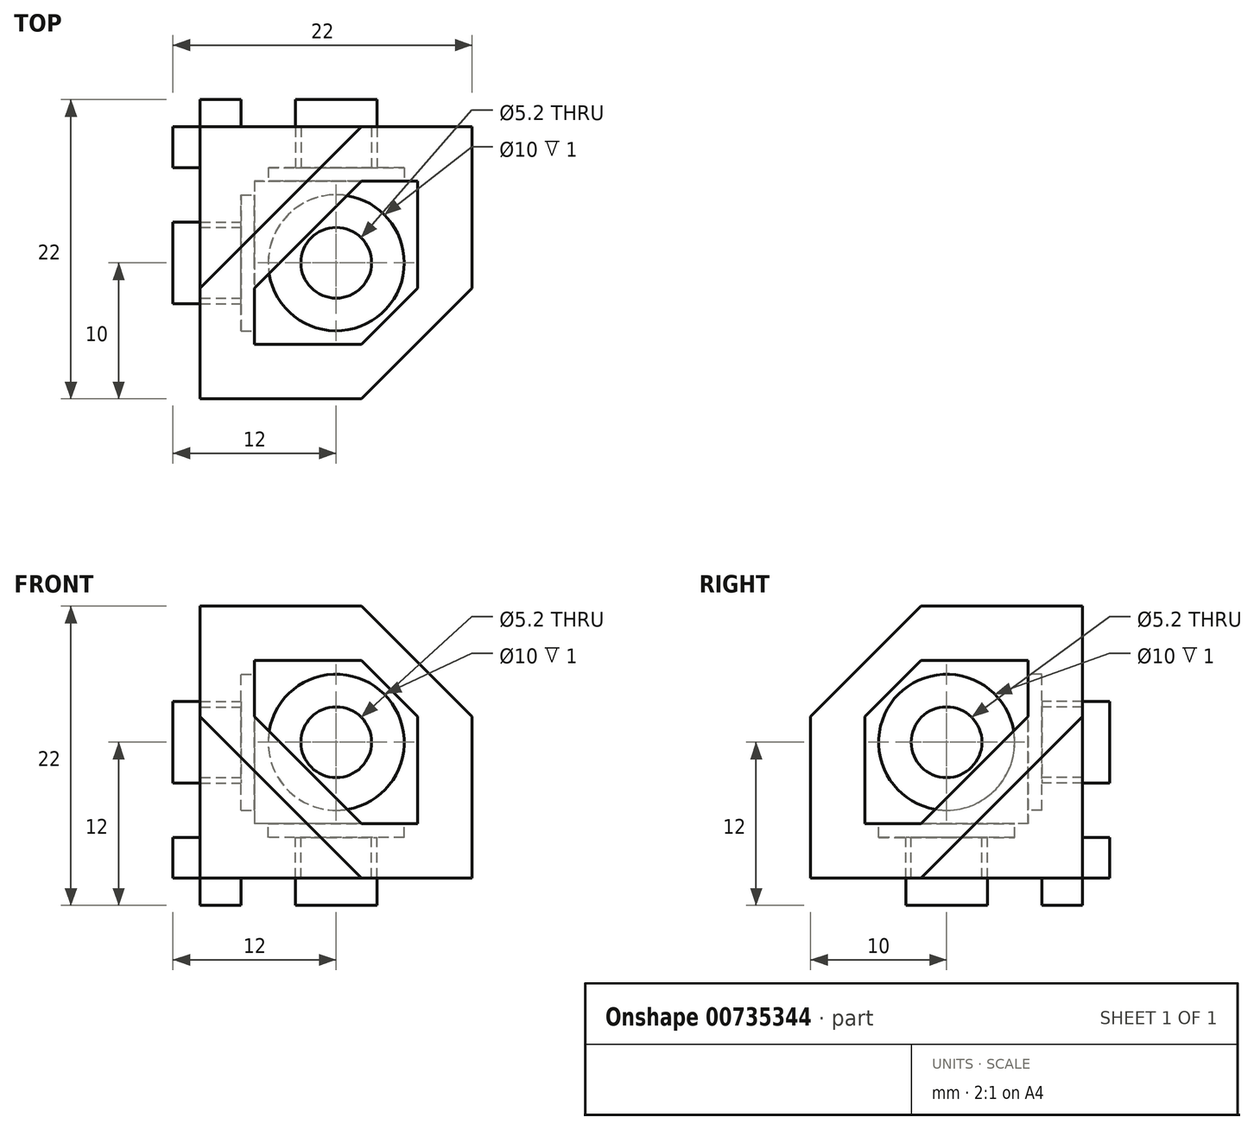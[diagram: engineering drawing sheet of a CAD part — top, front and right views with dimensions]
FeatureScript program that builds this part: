
annotation { "Feature Type Name" : "Feature", "Feature Type Description" : "" }
export const myFeature = defineFeature(function(context is Context, id is Id, definition is map)
    precondition{}
    {
        {
            var Q0;
            Q0=qCreatedBy(makeId("Front.planeOp"),FACE);
            var sketch = newSketch(context, id + "F0", { "sketchPlane" : qUnion([Q0])});
            skLineSegment(sketch, "E0.bottom", {"start": v(0, 0) * mm, "end": v(20, 0) * mm});
            skLineSegment(sketch, "E0.top", {"start": v(0, 20) * mm, "end": v(20, 20) * mm});
            skLineSegment(sketch, "E0.left", {"start": v(0, 0) * mm, "end": v(0, 20) * mm});
            skLineSegment(sketch, "E0.right", {"start": v(20, 0) * mm, "end": v(20, 20) * mm});
            skSolve(sketch);
        }
        {
            var Q0;
            Q0=makeQuery(id+"F0.imprint","IMPRINT",FACE,{"disambiguationData":[TD([[makeQuery(id+"F0.imprint","IMPRINT",EDGE,{"derivedFrom":sQuery(id+"F0.wireOp",EDGE,"E0.bottom")}),1.0]])]});
            extrude(context, id + "F1", {"entities" : qUnion([Q0]), "depth" : 20 * mm, "offsetDistance" : 25 * mm});
        }
        {
            var Q0;
            Q0=makeQuery(id+"F1.opExtrude","CAP_FACE",FACE,{"disambiguationData":[OSD([sQuery(id+"F0.wireOp",EDGE,"E0.bottom"),sQuery(id+"F0.wireOp",EDGE,"E0.top"),sQuery(id+"F0.wireOp",EDGE,"E0.left"),sQuery(id+"F0.wireOp",EDGE,"E0.right")])],"isStart":false});
            var sketch = newSketch(context, id + "F2", { "sketchPlane" : qUnion([Q0])});
            skLineSegment(sketch, "E1.bottom", {"start": v(20, 20) * mm, "end": v(4, 20) * mm});
            skLineSegment(sketch, "E1.top", {"start": v(20, 4) * mm, "end": v(4, 4) * mm});
            skLineSegment(sketch, "E1.left", {"start": v(20, 20) * mm, "end": v(20, 4) * mm});
            skLineSegment(sketch, "E1.right", {"start": v(4, 20) * mm, "end": v(4, 4) * mm});
            skSolve(sketch);
        }
        {
            var Q0;
            Q0=makeQuery(id+"F2.imprint","IMPRINT",FACE,{"disambiguationData":[TD([[makeQuery(id+"F2.imprint","IMPRINT",EDGE,{"derivedFrom":sQuery(id+"F2.wireOp",EDGE,"E1.bottom")}),-1.0]])]});
            extrude(context, id + "F3", {"entities" : qUnion([Q0]), "operationType" : NewBodyOperationType.REMOVE, "oppositeDirection" : true, "depth" : 16 * mm, "offsetDistance" : 25 * mm});
        }
        {
            var Q0;
            Q0=makeQuery(id+"F3.boolean.opBoolean","COPY",FACE,{"derivedFrom":makeQuery(id+"F3.opExtrude","CAP_FACE",FACE,{"disambiguationData":[OSD([sQuery(id+"F2.wireOp",EDGE,"E1.bottom"),sQuery(id+"F2.wireOp",EDGE,"E1.top"),sQuery(id+"F2.wireOp",EDGE,"E1.left"),sQuery(id+"F2.wireOp",EDGE,"E1.right")])],"isStart":false})});
            var sketch = newSketch(context, id + "F4", { "sketchPlane" : qUnion([Q0])});
            skPoint(sketch, "E2", {"position": v(10, 10) * mm});
            skSolve(sketch);
        }
        {
            var Q0;
            Q0=makeQuery(id+"F3.boolean.opBoolean","COPY",FACE,{"derivedFrom":makeQuery(id+"F3.opExtrude","SWEPT_FACE",FACE,{"disambiguationData":[OSD([sQuery(id+"F2.wireOp",EDGE,"E1.right")])]})});
            var sketch = newSketch(context, id + "F5", { "sketchPlane" : qUnion([Q0])});
            skPoint(sketch, "E3", {"position": v(-10, 10) * mm});
            skSolve(sketch);
        }
        {
            var Q0;
            Q0=makeQuery(id+"F3.boolean.opBoolean","COPY",FACE,{"derivedFrom":makeQuery(id+"F3.opExtrude","SWEPT_FACE",FACE,{"disambiguationData":[OSD([sQuery(id+"F2.wireOp",EDGE,"E1.top")])]})});
            var sketch = newSketch(context, id + "F6", { "sketchPlane" : qUnion([Q0])});
            skPoint(sketch, "E4", {"position": v(10, -10) * mm});
            skSolve(sketch);
        }
        {
            var Q0;
            Q0=makeQuery(id+"F1.opExtrude","CAP_FACE",FACE,{"disambiguationData":[OSD([sQuery(id+"F0.wireOp",EDGE,"E0.bottom"),sQuery(id+"F0.wireOp",EDGE,"E0.top"),sQuery(id+"F0.wireOp",EDGE,"E0.left"),sQuery(id+"F0.wireOp",EDGE,"E0.right")])],"isStart":false});
            var sketch = newSketch(context, id + "F7", { "sketchPlane" : qUnion([Q0])});
            skLineSegment(sketch, "E5", {"start": v(4, 20) * mm, "end": v(20, 4) * mm});
            skLineSegment(sketch, "E6", {"start": v(20, 4) * mm, "end": v(4, 4) * mm});
            skLineSegment(sketch, "E7", {"start": v(4, 4) * mm, "end": v(4, 20) * mm});
            skSolve(sketch);
        }
        {
            var Q0;
            Q0=makeQuery(id+"F1.opExtrude","SWEPT_FACE",FACE,{"disambiguationData":[OSD([sQuery(id+"F0.wireOp",EDGE,"E0.top")])]});
            var sketch = newSketch(context, id + "F8", { "sketchPlane" : qUnion([Q0])});
            skLineSegment(sketch, "E8", {"start": v(4, -4) * mm, "end": v(4, -20) * mm});
            skLineSegment(sketch, "E9", {"start": v(4, -20) * mm, "end": v(20, -4) * mm});
            skLineSegment(sketch, "E10", {"start": v(20, -4) * mm, "end": v(4, -4) * mm});
            skSolve(sketch);
        }
        {
            var Q0;
            Q0=makeQuery(id+"F1.opExtrude","SWEPT_FACE",FACE,{"disambiguationData":[OSD([sQuery(id+"F0.wireOp",EDGE,"E0.right")])]});
            var sketch = newSketch(context, id + "F9", { "sketchPlane" : qUnion([Q0])});
            skLineSegment(sketch, "E11", {"start": v(-4, 20) * mm, "end": v(-20, 4) * mm});
            skLineSegment(sketch, "E12", {"start": v(-20, 4) * mm, "end": v(-4, 4) * mm});
            skLineSegment(sketch, "E13", {"start": v(-4, 4) * mm, "end": v(-4, 20) * mm});
            skSolve(sketch);
        }
        {
            var Q0;
            Q0=makeQuery(id+"F7.imprint","IMPRINT",FACE,{"disambiguationData":[TD([[makeQuery(id+"F7.imprint","IMPRINT",EDGE,{"derivedFrom":sQuery(id+"F7.wireOp",EDGE,"E5")}),-1.0]])]});
            extrude(context, id + "F10", {"entities" : qUnion([Q0]), "operationType" : NewBodyOperationType.ADD, "oppositeDirection" : true, "depth" : 4 * mm, "offsetDistance" : 25 * mm});
        }
        {
            var Q0;
            Q0=makeQuery(id+"F8.imprint","IMPRINT",FACE,{"disambiguationData":[TD([[makeQuery(id+"F8.imprint","IMPRINT",EDGE,{"derivedFrom":sQuery(id+"F8.wireOp",EDGE,"E8")}),1.0]])]});
            extrude(context, id + "F11", {"entities" : qUnion([Q0]), "operationType" : NewBodyOperationType.ADD, "oppositeDirection" : true, "depth" : 4 * mm, "offsetDistance" : 25 * mm});
        }
        {
            var Q0;
            Q0=makeQuery(id+"F9.imprint","IMPRINT",FACE,{"disambiguationData":[TD([[makeQuery(id+"F9.imprint","IMPRINT",EDGE,{"derivedFrom":sQuery(id+"F9.wireOp",EDGE,"E11")}),1.0]])]});
            extrude(context, id + "F12", {"entities" : qUnion([Q0]), "operationType" : NewBodyOperationType.ADD, "oppositeDirection" : true, "depth" : 4 * mm, "offsetDistance" : 25 * mm});
        }
        {
            var Q0;
            Q0=sQuery(id+"F4.wireOp",VERTEX,"E2");
            var Q1;
            Q1=sQuery(id+"F6.wireOp",VERTEX,"E4");
            var Q2;
            Q2=sQuery(id+"F5.wireOp",VERTEX,"E3");
            var Q3;
            Q3=makeQuery(id+"F1.opExtrude","SWEPT_BODY",BODY,{"disambiguationData":[OSD([sQuery(id+"F0.wireOp",EDGE,"E0.bottom"),sQuery(id+"F0.wireOp",EDGE,"E0.top"),sQuery(id+"F0.wireOp",EDGE,"E0.left"),sQuery(id+"F0.wireOp",EDGE,"E0.right")])]});
            hole(context, id + "F13", {"style" : HoleStyle.C_BORE, "endStyle" : HoleEndStyle.THROUGH, "holeDiameter" : 5.2 * mm, "cBoreDiameter" : 10 * mm, "cBoreDepth" : 1 * mm, "majorDiameter" : 5 * mm, "isTappedThrough" : true, "tappedDepth" : 12 * mm, "tapClearance" : 3, "locations" : qUnion([Q0, Q1, Q2]), "scope" : qUnion([Q3])});
        }
        {
            var Q0;
            {var subQ0=sQuery(id+"F0.wireOp",EDGE,"E0.top");Q0=makeQuery(id+"F11.boolean.opBoolean","MERGE",VERTEX,{"derivedFrom":[makeQuery(id+"F10.boolean.opBoolean","MERGE",VERTEX,{"derivedFrom":[makeQuery(id+"F3.boolean.opBoolean","COPY",VERTEX,{"derivedFrom":makeQuery(id+"F3.opExtrude","CAP_VERTEX",VERTEX,{"disambiguationData":[OSD([subQ0,sQuery(id+"F2.wireOp",EDGE,"E1.bottom"),sQuery(id+"F2.wireOp",EDGE,"E1.right")])],"isStart":true})}),makeQuery(id+"F10.opExtrude","CAP_VERTEX",VERTEX,{"disambiguationData":[OSD([subQ0,sQuery(id+"F7.wireOp",EDGE,"E5"),sQuery(id+"F7.wireOp",EDGE,"E7")])],"isStart":true})]}),makeQuery(id+"F11.opExtrude","CAP_VERTEX",VERTEX,{"disambiguationData":[OSD([subQ0,sQuery(id+"F8.wireOp",EDGE,"E8"),sQuery(id+"F8.wireOp",EDGE,"E9")])],"isStart":true})]});}
            var Q1;
            {var subQ0=sQuery(id+"F0.wireOp",EDGE,"E0.right");var subQ1=sQuery(id+"F0.wireOp",EDGE,"E0.top");Q1=makeQuery(id+"F12.boolean.opBoolean","MERGE",VERTEX,{"derivedFrom":[makeQuery(id+"F11.boolean.opBoolean","MERGE",VERTEX,{"derivedFrom":[makeQuery(id+"F3.boolean.opBoolean","COPY",VERTEX,{"derivedFrom":makeQuery(id+"F3.opExtrude","CAP_VERTEX",VERTEX,{"disambiguationData":[OSD([sQuery(id+"F2.wireOp",EDGE,"E1.bottom"),sQuery(id+"F2.wireOp",EDGE,"E1.left")])],"isStart":false})}),makeQuery(id+"F11.opExtrude","CAP_VERTEX",VERTEX,{"disambiguationData":[OSD([subQ1,subQ0,sQuery(id+"F8.wireOp",EDGE,"E9"),sQuery(id+"F8.wireOp",EDGE,"E10")])],"isStart":true})]}),makeQuery(id+"F12.opExtrude","CAP_VERTEX",VERTEX,{"disambiguationData":[OSD([subQ1,subQ0,sQuery(id+"F9.wireOp",EDGE,"E11"),sQuery(id+"F9.wireOp",EDGE,"E13")])],"isStart":true})]});}
            var Q2;
            {var subQ0=sQuery(id+"F0.wireOp",EDGE,"E0.right");Q2=makeQuery(id+"F12.boolean.opBoolean","MERGE",VERTEX,{"derivedFrom":[makeQuery(id+"F10.boolean.opBoolean","MERGE",VERTEX,{"derivedFrom":[makeQuery(id+"F3.boolean.opBoolean","COPY",VERTEX,{"derivedFrom":makeQuery(id+"F3.opExtrude","CAP_VERTEX",VERTEX,{"disambiguationData":[OSD([subQ0,sQuery(id+"F2.wireOp",EDGE,"E1.top"),sQuery(id+"F2.wireOp",EDGE,"E1.left")])],"isStart":true})}),makeQuery(id+"F10.opExtrude","CAP_VERTEX",VERTEX,{"disambiguationData":[OSD([subQ0,sQuery(id+"F7.wireOp",EDGE,"E5"),sQuery(id+"F7.wireOp",EDGE,"E6")])],"isStart":true})]}),makeQuery(id+"F12.opExtrude","CAP_VERTEX",VERTEX,{"disambiguationData":[OSD([subQ0,sQuery(id+"F9.wireOp",EDGE,"E11"),sQuery(id+"F9.wireOp",EDGE,"E12")])],"isStart":true})]});}
            cPlane(context, id + "F14", {"entities" : qUnion([Q0, Q1, Q2]), "cplaneType" : CPlaneType.THREE_POINT, "offset" : 25 * mm, "width" : 150 * mm, "height" : 150 * mm});
        }
        {
            var Q0;
            Q0=qCreatedBy(id+"F14.planeOp",FACE);
            var sketch = newSketch(context, id + "F15", { "sketchPlane" : qUnion([Q0])});
            skLineSegment(sketch, "E14.bottom", {"start": v(-25.78, 18.29) * mm, "end": v(26.3, 18.29) * mm});
            skLineSegment(sketch, "E14.top", {"start": v(-25.78, -20.5) * mm, "end": v(26.3, -20.5) * mm});
            skLineSegment(sketch, "E14.left", {"start": v(-25.78, 18.29) * mm, "end": v(-25.78, -20.5) * mm});
            skLineSegment(sketch, "E14.right", {"start": v(26.3, 18.29) * mm, "end": v(26.3, -20.5) * mm});
            skSolve(sketch);
        }
        {
            var Q0;
            Q0=makeQuery(id+"F15.imprint","IMPRINT",FACE,{"disambiguationData":[TD([[makeQuery(id+"F15.imprint","IMPRINT",EDGE,{"derivedFrom":sQuery(id+"F15.wireOp",EDGE,"E14.bottom")}),-1.0]])]});
            extrude(context, id + "F16", {"entities" : qUnion([Q0]), "operationType" : NewBodyOperationType.REMOVE, "depth" : 10 * mm, "offsetDistance" : 25 * mm, "hasSecondDirection" : true, "secondDirectionOppositeDirection" : true, "secondDirectionDepth" : 7 * mm});
        }
        {
            var Q0;
            Q0=makeQuery(id+"F1.opExtrude","SWEPT_FACE",FACE,{"disambiguationData":[OSD([sQuery(id+"F0.wireOp",EDGE,"E0.left")])]});
            var sketch = newSketch(context, id + "F17", { "sketchPlane" : qUnion([Q0])});
            skLineSegment(sketch, "E15.bottom", {"start": v(7, 0) * mm, "end": v(13, 0) * mm});
            skLineSegment(sketch, "E15.top", {"start": v(7, 3) * mm, "end": v(13, 3) * mm});
            skLineSegment(sketch, "E15.left", {"start": v(7, 0) * mm, "end": v(7, 3) * mm});
            skLineSegment(sketch, "E15.right", {"start": v(13, 0) * mm, "end": v(13, 3) * mm});
            skLineSegment(sketch, "E16.bottom", {"start": v(0, 13) * mm, "end": v(3, 13) * mm});
            skLineSegment(sketch, "E16.top", {"start": v(0, 7) * mm, "end": v(3, 7) * mm});
            skLineSegment(sketch, "E16.left", {"start": v(0, 13) * mm, "end": v(0, 7) * mm});
            skLineSegment(sketch, "E16.right", {"start": v(3, 13) * mm, "end": v(3, 7) * mm});
            skPoint(sketch, "E17", {"position": v(3, 10) * mm});
            skPoint(sketch, "E18", {"position": v(10, 3) * mm});
            skPoint(sketch, "E19", {"position": v(10, 0) * mm});
            skPoint(sketch, "E20", {"position": v(0, 10) * mm});
            skSolve(sketch);
        }
        {
            var Q0;
            Q0=makeQuery(id+"F17.imprint","IMPRINT",FACE,{"disambiguationData":[TD([[makeQuery(id+"F17.imprint","IMPRINT",EDGE,{"derivedFrom":sQuery(id+"F17.wireOp",EDGE,"E16.bottom")}),-1.0]])]});
            var Q1;
            Q1=makeQuery(id+"F17.imprint","IMPRINT",FACE,{"disambiguationData":[TD([[makeQuery(id+"F17.imprint","IMPRINT",EDGE,{"derivedFrom":sQuery(id+"F17.wireOp",EDGE,"E15.bottom")}),-1.0]])]});
            extrude(context, id + "F18", {"entities" : qUnion([Q0, Q1]), "operationType" : NewBodyOperationType.ADD, "depth" : 2 * mm, "offsetDistance" : 25 * mm});
        }
        {
            var Q0;
            Q0=makeQuery(id+"F18.boolean.opBoolean","MERGE",FACE,{"derivedFrom":[makeQuery(id+"F1.opExtrude","SWEPT_FACE",FACE,{"disambiguationData":[OSD([sQuery(id+"F0.wireOp",EDGE,"E0.bottom")])]}),makeQuery(id+"F18.opExtrude","SWEPT_FACE",FACE,{"disambiguationData":[OSD([sQuery(id+"F17.wireOp",EDGE,"E15.bottom")])]})]});
            var sketch = newSketch(context, id + "F19", { "sketchPlane" : qUnion([Q0])});
            skLineSegment(sketch, "E21.bottom", {"start": v(7, 0) * mm, "end": v(13, 0) * mm});
            skLineSegment(sketch, "E21.top", {"start": v(7, 3) * mm, "end": v(13, 3) * mm});
            skLineSegment(sketch, "E21.left", {"start": v(7, 0) * mm, "end": v(7, 3) * mm});
            skLineSegment(sketch, "E21.right", {"start": v(13, 0) * mm, "end": v(13, 3) * mm});
            skPoint(sketch, "E22", {"position": v(10, 3) * mm});
            skPoint(sketch, "E23", {"position": v(10, 0) * mm});
            skLineSegment(sketch, "E24.bottom", {"start": v(0, 13) * mm, "end": v(3, 13) * mm});
            skLineSegment(sketch, "E24.top", {"start": v(0, 7) * mm, "end": v(3, 7) * mm});
            skLineSegment(sketch, "E24.left", {"start": v(0, 13) * mm, "end": v(0, 7) * mm});
            skLineSegment(sketch, "E24.right", {"start": v(3, 13) * mm, "end": v(3, 7) * mm});
            skSolve(sketch);
        }
        {
            var Q0;
            Q0=makeQuery(id+"F19.imprint","IMPRINT",FACE,{"disambiguationData":[TD([[makeQuery(id+"F19.imprint","IMPRINT",EDGE,{"derivedFrom":sQuery(id+"F19.wireOp",EDGE,"E21.bottom")}),1.0]])]});
            var Q1;
            Q1=makeQuery(id+"F19.imprint","IMPRINT",FACE,{"disambiguationData":[TD([[makeQuery(id+"F19.imprint","IMPRINT",EDGE,{"derivedFrom":sQuery(id+"F19.wireOp",EDGE,"E24.bottom")}),-1.0]])]});
            extrude(context, id + "F20", {"entities" : qUnion([Q0, Q1]), "operationType" : NewBodyOperationType.ADD, "depth" : 2 * mm, "offsetDistance" : 25 * mm});
        }
        {
            var Q0;
            Q0=makeQuery(id+"F20.boolean.opBoolean","MERGE",FACE,{"derivedFrom":[makeQuery(id+"F18.boolean.opBoolean","MERGE",FACE,{"derivedFrom":[makeQuery(id+"F1.opExtrude","CAP_FACE",FACE,{"disambiguationData":[OSD([sQuery(id+"F0.wireOp",EDGE,"E0.bottom"),sQuery(id+"F0.wireOp",EDGE,"E0.top"),sQuery(id+"F0.wireOp",EDGE,"E0.left"),sQuery(id+"F0.wireOp",EDGE,"E0.right")])],"isStart":true}),makeQuery(id+"F18.opExtrude","SWEPT_FACE",FACE,{"disambiguationData":[OSD([sQuery(id+"F17.wireOp",EDGE,"E16.left")])]})]}),makeQuery(id+"F20.opExtrude","SWEPT_FACE",FACE,{"disambiguationData":[OSD([sQuery(id+"F19.wireOp",EDGE,"E21.bottom")])]})]});
            var sketch = newSketch(context, id + "F21", { "sketchPlane" : qUnion([Q0])});
            skLineSegment(sketch, "E25.bottom", {"start": v(0, 13) * mm, "end": v(-3, 13) * mm});
            skLineSegment(sketch, "E25.top", {"start": v(0, 7) * mm, "end": v(-3, 7) * mm});
            skLineSegment(sketch, "E25.left", {"start": v(0, 13) * mm, "end": v(0, 7) * mm});
            skLineSegment(sketch, "E25.right", {"start": v(-3, 13) * mm, "end": v(-3, 7) * mm});
            skLineSegment(sketch, "E26.bottom", {"start": v(-7, 0) * mm, "end": v(-13, 0) * mm});
            skLineSegment(sketch, "E26.top", {"start": v(-7, 3) * mm, "end": v(-13, 3) * mm});
            skLineSegment(sketch, "E26.left", {"start": v(-7, 0) * mm, "end": v(-7, 3) * mm});
            skLineSegment(sketch, "E26.right", {"start": v(-13, 0) * mm, "end": v(-13, 3) * mm});
            skSolve(sketch);
        }
        {
            var Q0;
            Q0=makeQuery(id+"F21.imprint","IMPRINT",FACE,{"disambiguationData":[TD([[makeQuery(id+"F21.imprint","IMPRINT",EDGE,{"derivedFrom":sQuery(id+"F21.wireOp",EDGE,"E25.bottom")}),1.0]])]});
            var Q1;
            Q1=makeQuery(id+"F21.imprint","IMPRINT",FACE,{"disambiguationData":[TD([[makeQuery(id+"F21.imprint","IMPRINT",EDGE,{"derivedFrom":sQuery(id+"F21.wireOp",EDGE,"E26.bottom")}),-1.0]])]});
            extrude(context, id + "F22", {"entities" : qUnion([Q0, Q1]), "operationType" : NewBodyOperationType.ADD, "depth" : 2 * mm, "offsetDistance" : 25 * mm});
        }
    });
